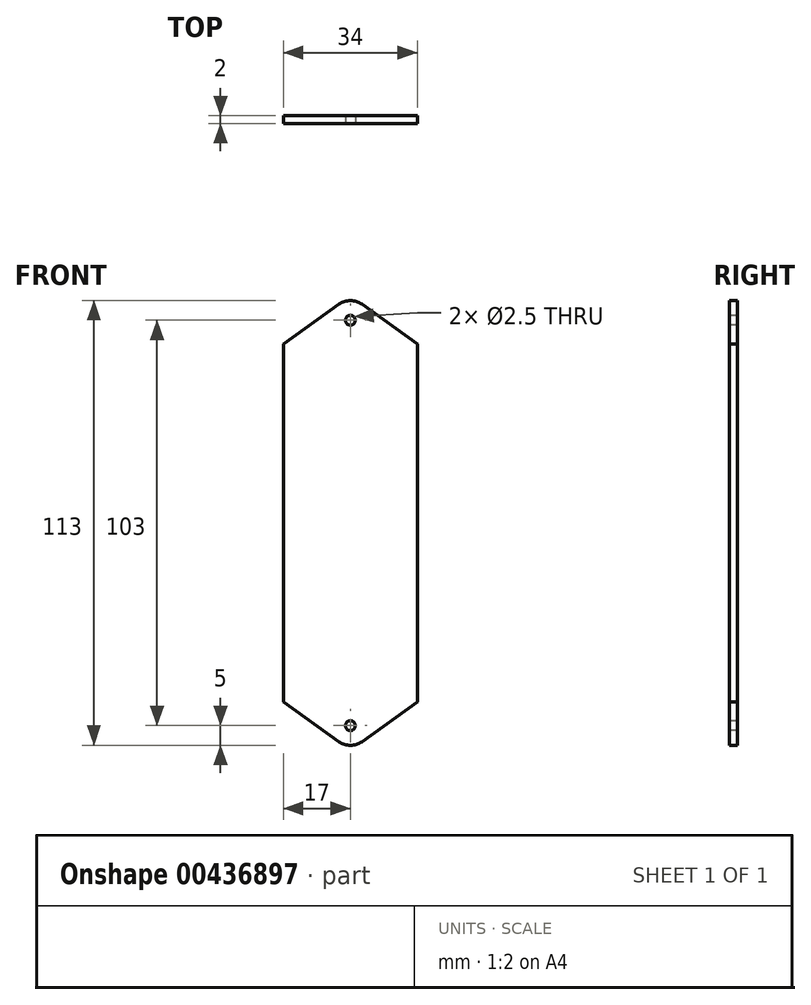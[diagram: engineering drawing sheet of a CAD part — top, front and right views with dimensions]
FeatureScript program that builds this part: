
annotation { "Feature Type Name" : "Feature", "Feature Type Description" : "" }
export const myFeature = defineFeature(function(context is Context, id is Id, definition is map)
    precondition{}
    {
        {
            var Q0;
            Q0=qCreatedBy(makeId("Front.planeOp"),FACE);
            var sketch = newSketch(context, id + "F0", { "sketchPlane" : qUnion([Q0])});
            skLineSegment(sketch, "E0.left", {"start": v(0, 0) * mm, "end": v(0, 91) * mm});
            skLineSegment(sketch, "E0.right", {"start": v(34, 0) * mm, "end": v(34, 91) * mm});
            skLineSegment(sketch, "E1", {"start": v(0, 91) * mm, "end": v(14.1, 101.07) * mm});
            skPoint(sketch, "E1.endSnap0", {"position": v(17, 91) * mm});
            skLineSegment(sketch, "E2", {"start": v(19.9, 101.07) * mm, "end": v(34, 91) * mm});
            skPoint(sketch, "E3.visualSharp", {"position": v(17, 103.14) * mm});
            skArc(sketch, "E3.filletArc", {"start": v(19.9, 101.07) * mm, "mid": v(17, 102) * mm, "end": v(14.1, 101.07) * mm});
            skLineSegment(sketch, "E4", {"start": v(34, 0) * mm, "end": v(19.9, -10.07) * mm});
            skPoint(sketch, "E4.endSnap0", {"position": v(17, 0) * mm});
            skLineSegment(sketch, "E5", {"start": v(14.1, -10.07) * mm, "end": v(0, 0) * mm});
            skPoint(sketch, "E6.visualSharp", {"position": v(17, -12.14) * mm});
            skArc(sketch, "E6.filletArc", {"start": v(14.1, -10.07) * mm, "mid": v(17, -11) * mm, "end": v(19.9, -10.07) * mm});
            skSolve(sketch);
        }
        {
            var Q0;
            Q0 = qSketchRegion(id + "F0", true);
            extrude(context, id + "F1", {"entities" : qUnion([Q0]), "depth" : 2 * mm});
        }
        {
            var Q0;
            Q0=makeQuery(id+"F1.opExtrude","CAP_FACE",FACE,{"disambiguationData":[OSD([sQuery(id+"F0.wireOp",EDGE,"E0.left"),sQuery(id+"F0.wireOp",EDGE,"E0.right"),sQuery(id+"F0.wireOp",EDGE,"E1"),sQuery(id+"F0.wireOp",EDGE,"E2"),sQuery(id+"F0.wireOp",EDGE,"E3.filletArc"),sQuery(id+"F0.wireOp",EDGE,"E4"),sQuery(id+"F0.wireOp",EDGE,"E5"),sQuery(id+"F0.wireOp",EDGE,"E6.filletArc")])],"isStart":false});
            var sketch = newSketch(context, id + "F2", { "sketchPlane" : qUnion([Q0])});
            skPoint(sketch, "E7", {"position": v(17, 97) * mm});
            skPoint(sketch, "E8", {"position": v(17, -6) * mm});
            skSolve(sketch);
        }
        {
            var Q0;
            Q0=sQuery(id+"F2.wireOp",VERTEX,"E8");
            var Q1;
            Q1=sQuery(id+"F2.wireOp",VERTEX,"E7");
            var Q2;
            Q2=makeQuery(id+"F1.opExtrude","SWEPT_BODY",BODY,{"disambiguationData":[OSD([sQuery(id+"F0.wireOp",EDGE,"E0.left"),sQuery(id+"F0.wireOp",EDGE,"E0.right"),sQuery(id+"F0.wireOp",EDGE,"E1"),sQuery(id+"F0.wireOp",EDGE,"E2"),sQuery(id+"F0.wireOp",EDGE,"E3.filletArc"),sQuery(id+"F0.wireOp",EDGE,"E4"),sQuery(id+"F0.wireOp",EDGE,"E5"),sQuery(id+"F0.wireOp",EDGE,"E6.filletArc")])]});
            hole(context, id + "F3", {"style" : HoleStyle.SIMPLE, "endStyle" : HoleEndStyle.THROUGH, "standardTappedOrClearance" : lookupTablePath({ "standard" : "ISO", "engagement" : "75%", "pitch" : "0.5 mm", "size" : "M3", "type" : "Tapped" }), "standardBlindInLast" : lookupTablePath({ "standard" : "ISO", "engagement" : "75%", "pitch" : "0.5 mm", "size" : "M3", "type" : "Tapped" }), "holeDiameter" : 2.5 * mm, "showTappedDepth" : true, "isTappedThrough" : true, "tappedDepth" : 12 * mm, "tapClearance" : 3, "locations" : qUnion([Q0, Q1]), "scope" : qUnion([Q2]), "majorDiameter" : 3 * mm});
        }
    });
